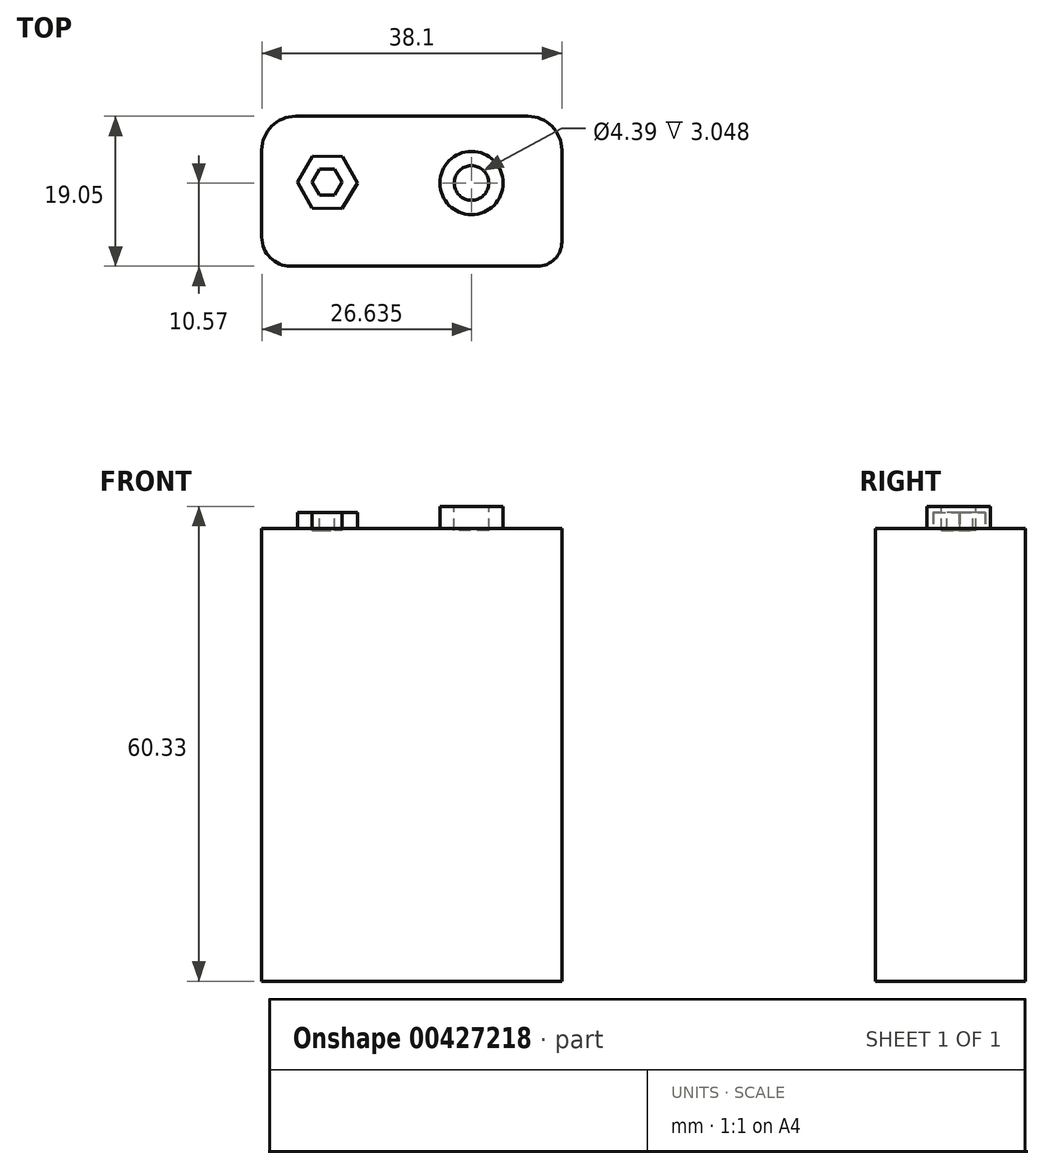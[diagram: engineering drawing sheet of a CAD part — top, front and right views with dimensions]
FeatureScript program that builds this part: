
annotation { "Feature Type Name" : "Feature", "Feature Type Description" : "" }
export const myFeature = defineFeature(function(context is Context, id is Id, definition is map)
    precondition{}
    {
        {
            var Q0;
            Q0=qCreatedBy(makeId("Front.planeOp"),FACE);
            var sketch = newSketch(context, id + "F0", { "sketchPlane" : qUnion([Q0])});
            skLineSegment(sketch, "E0.bottom", {"start": v(19.05, 28.77) * mm, "end": v(-19.05, 28.77) * mm});
            skLineSegment(sketch, "E0.top", {"start": v(19.05, -28.77) * mm, "end": v(-19.05, -28.77) * mm});
            skLineSegment(sketch, "E0.left", {"start": v(19.05, 28.77) * mm, "end": v(19.05, -28.77) * mm});
            skLineSegment(sketch, "E0.right", {"start": v(-19.05, 28.77) * mm, "end": v(-19.05, -28.77) * mm});
            skPoint(sketch, "E0.middle", {"position": v(0, 0) * mm});
            skSolve(sketch);
        }
        {
            var Q0;
            Q0 = qSketchRegion(id + "F0", true);
            extrude(context, id + "F1", {"entities" : qUnion([Q0]), "depth" : 19.05 * mm});
        }
        {
            var Q0;
            Q0=makeQuery(id+"F1.opExtrude","CAP_EDGE",EDGE,{"disambiguationData":[OSD([sQuery(id+"F0.wireOp",EDGE,"E0.left")])],"isStart":false});
            fillet(context, id + "F2", {"entities" : qUnion([Q0]), "radius" : 3.07 * mm, "tangentPropagation" : true, "allowEdgeOverflow" : false});
        }
        {
            var Q0;
            Q0=makeQuery(id+"F1.opExtrude","CAP_EDGE",EDGE,{"disambiguationData":[OSD([sQuery(id+"F0.wireOp",EDGE,"E0.right")])],"isStart":false});
            fillet(context, id + "F3", {"entities" : qUnion([Q0]), "radius" : 3.68 * mm, "tangentPropagation" : true, "allowEdgeOverflow" : false});
        }
        {
            var Q0;
            Q0=makeQuery(id+"F1.opExtrude","CAP_EDGE",EDGE,{"disambiguationData":[OSD([sQuery(id+"F0.wireOp",EDGE,"E0.left")])],"isStart":true});
            fillet(context, id + "F4", {"entities" : qUnion([Q0]), "radius" : 4.3 * mm, "tangentPropagation" : true, "allowEdgeOverflow" : false});
        }
        {
            var Q0;
            Q0=makeQuery(id+"F1.opExtrude","CAP_EDGE",EDGE,{"disambiguationData":[OSD([sQuery(id+"F0.wireOp",EDGE,"E0.right")])],"isStart":true});
            fillet(context, id + "F5", {"entities" : qUnion([Q0]), "radius" : 4.3 * mm, "tangentPropagation" : true, "allowEdgeOverflow" : false});
        }
        {
            var Q0;
            Q0=makeQuery(id+"F1.opExtrude","SWEPT_FACE",FACE,{"disambiguationData":[OSD([sQuery(id+"F0.wireOp",EDGE,"E0.bottom")])]});
            var sketch = newSketch(context, id + "F6", { "sketchPlane" : qUnion([Q0])});
            skCircle(sketch, "E1.cCircle", {"center": v(-10.73, -8.42) * mm, "radius": 3.8 * mm, "construction": true});
            skLineSegment(sketch, "E1.0", {"start": v(-8.88, -11.75) * mm, "end": v(-12.69, -11.68) * mm});
            skLineSegment(sketch, "E1.1", {"start": v(-12.69, -11.68) * mm, "end": v(-14.54, -8.35) * mm});
            skLineSegment(sketch, "E1.2", {"start": v(-14.54, -8.35) * mm, "end": v(-12.58, -5.09) * mm});
            skLineSegment(sketch, "E1.3", {"start": v(-12.58, -5.09) * mm, "end": v(-8.77, -5.15) * mm});
            skLineSegment(sketch, "E1.4", {"start": v(-8.77, -5.15) * mm, "end": v(-6.92, -8.48) * mm});
            skLineSegment(sketch, "E1.5", {"start": v(-6.92, -8.48) * mm, "end": v(-8.88, -11.75) * mm});
            skSolve(sketch);
        }
        {
            var Q0;
            Q0 = qSketchRegion(id + "F6", true);
            extrude(context, id + "F7", {"entities" : qUnion([Q0]), "operationType" : NewBodyOperationType.ADD, "depth" : 2.03 * mm});
        }
        {
            var Q0;
            Q0=makeQuery(id+"F1.opExtrude","SWEPT_FACE",FACE,{"disambiguationData":[OSD([sQuery(id+"F0.wireOp",EDGE,"E0.bottom")])]});
            var sketch = newSketch(context, id + "F8", { "sketchPlane" : qUnion([Q0])});
            skCircle(sketch, "E2", {"center": v(7.58, -8.48) * mm, "radius": 4.02 * mm});
            skSolve(sketch);
        }
        {
            var Q0;
            Q0 = qSketchRegion(id + "F8", true);
            extrude(context, id + "F9", {"entities" : qUnion([Q0]), "operationType" : NewBodyOperationType.ADD, "depth" : 2.8 * mm});
        }
        {
            var Q0;
            Q0=makeQuery(id+"F7.opExtrude","CAP_FACE",FACE,{"disambiguationData":[OSD([sQuery(id+"F6.wireOp",EDGE,"E1.0"),sQuery(id+"F6.wireOp",EDGE,"E1.1"),sQuery(id+"F6.wireOp",EDGE,"E1.2"),sQuery(id+"F6.wireOp",EDGE,"E1.3"),sQuery(id+"F6.wireOp",EDGE,"E1.4"),sQuery(id+"F6.wireOp",EDGE,"E1.5")])],"isStart":false});
            var sketch = newSketch(context, id + "F10", { "sketchPlane" : qUnion([Q0])});
            skCircle(sketch, "E3.cCircle", {"center": v(-10.78, -8.35) * mm, "radius": 1.9 * mm, "construction": true});
            skPoint(sketch, "E3.cCircle.centerSnap0", {"position": v(-10.78, -11.72) * mm});
            skLineSegment(sketch, "E3.0", {"start": v(-8.88, -8.35) * mm, "end": v(-9.83, -10) * mm});
            skLineSegment(sketch, "E3.1", {"start": v(-9.83, -10) * mm, "end": v(-11.74, -10) * mm});
            skLineSegment(sketch, "E3.2", {"start": v(-11.74, -10) * mm, "end": v(-12.69, -8.35) * mm});
            skLineSegment(sketch, "E3.3", {"start": v(-12.69, -8.35) * mm, "end": v(-11.74, -6.7) * mm});
            skLineSegment(sketch, "E3.4", {"start": v(-11.74, -6.7) * mm, "end": v(-9.83, -6.7) * mm});
            skLineSegment(sketch, "E3.5", {"start": v(-9.83, -6.7) * mm, "end": v(-8.88, -8.35) * mm});
            skSolve(sketch);
        }
        {
            var Q0;
            Q0 = qSketchRegion(id + "F10", true);
            extrude(context, id + "F11", {"entities" : qUnion([Q0]), "operationType" : NewBodyOperationType.REMOVE, "oppositeDirection" : true, "depth" : 2.3 * mm});
        }
        {
            var Q0;
            Q0=makeQuery(id+"F9.opExtrude","CAP_FACE",FACE,{"disambiguationData":[OSD([sQuery(id+"F8.wireOp",EDGE,"E2")])],"isStart":false});
            var sketch = newSketch(context, id + "F12", { "sketchPlane" : qUnion([Q0])});
            skCircle(sketch, "E4", {"center": v(7.58, -8.48) * mm, "radius": 2.2 * mm});
            skSolve(sketch);
        }
        {
            var Q0;
            Q0 = qSketchRegion(id + "F12", true);
            extrude(context, id + "F13", {"entities" : qUnion([Q0]), "operationType" : NewBodyOperationType.REMOVE, "oppositeDirection" : true, "depth" : 3.05 * mm});
        }
    });
